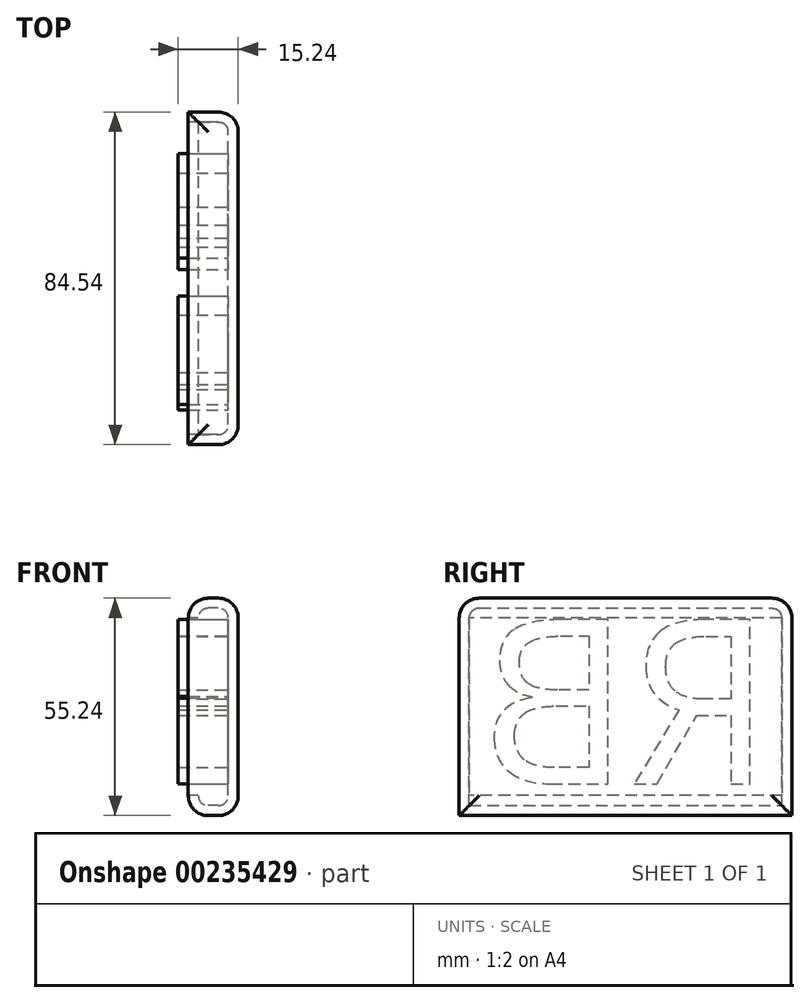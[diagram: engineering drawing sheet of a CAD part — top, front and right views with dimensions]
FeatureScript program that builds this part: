
annotation { "Feature Type Name" : "Feature", "Feature Type Description" : "" }
export const myFeature = defineFeature(function(context is Context, id is Id, definition is map)
    precondition{}
    {
        {
            var Q0;
            Q0=qCreatedBy(makeId("Right.planeOp"),FACE);
            var sketch = newSketch(context, id + "F0", { "sketchPlane" : qUnion([Q0])});
            skLineSegment(sketch, "E0.bottom", {"start": v(42.27, 27.62) * mm, "end": v(-42.27, 27.62) * mm});
            skLineSegment(sketch, "E0.top", {"start": v(42.27, -27.62) * mm, "end": v(-42.27, -27.62) * mm});
            skLineSegment(sketch, "E0.left", {"start": v(42.27, 27.62) * mm, "end": v(42.27, -27.62) * mm});
            skLineSegment(sketch, "E0.right", {"start": v(-42.27, 27.62) * mm, "end": v(-42.27, -27.62) * mm});
            skPoint(sketch, "E0.middle", {"position": v(0, 0) * mm});
            skSolve(sketch);
        }
        {
            var Q0;
            Q0=makeQuery(id+"F0.imprint","IMPRINT",FACE,{"disambiguationData":[TD([[makeQuery(id+"F0.imprint","IMPRINT",EDGE,{"derivedFrom":sQuery(id+"F0.wireOp",EDGE,"E0.bottom")}),1.0]])]});
            extrude(context, id + "F1", {"entities" : qUnion([Q0]), "depth" : 12.7 * mm});
        }
        {
            var Q0;
            Q0=makeQuery(id+"F1.opExtrude","SWEPT_FACE",FACE,{"disambiguationData":[OSD([sQuery(id+"F0.wireOp",EDGE,"E0.bottom")])]});
            var Q1;
            Q1=makeQuery(id+"F1.opExtrude","CAP_FACE",FACE,{"disambiguationData":[OSD([sQuery(id+"F0.wireOp",EDGE,"E0.bottom"),sQuery(id+"F0.wireOp",EDGE,"E0.top"),sQuery(id+"F0.wireOp",EDGE,"E0.left"),sQuery(id+"F0.wireOp",EDGE,"E0.right")])],"isStart":false});
            var Q2;
            Q2=makeQuery(id+"F1.opExtrude","CAP_EDGE",EDGE,{"disambiguationData":[OSD([sQuery(id+"F0.wireOp",EDGE,"E0.bottom")])],"isStart":false});
            fillet(context, id + "F2", {"entities" : qUnion([Q0, Q1, Q2]), "radius" : 5.08 * mm, "tangentPropagation" : true, "allowEdgeOverflow" : false});
        }
        {
            var Q0;
            Q0=makeQuery(id+"F1.opExtrude","CAP_EDGE",EDGE,{"disambiguationData":[OSD([sQuery(id+"F0.wireOp",EDGE,"E0.top")])],"isStart":true});
            fillet(context, id + "F3", {"entities" : qUnion([Q0]), "radius" : 5.08 * mm, "tangentPropagation" : true, "allowEdgeOverflow" : false});
        }
        {
            var Q0;
            Q0=makeQuery(id+"F1.opExtrude","CAP_FACE",FACE,{"disambiguationData":[OSD([sQuery(id+"F0.wireOp",EDGE,"E0.bottom"),sQuery(id+"F0.wireOp",EDGE,"E0.top"),sQuery(id+"F0.wireOp",EDGE,"E0.left"),sQuery(id+"F0.wireOp",EDGE,"E0.right")])],"isStart":true});
            shell(context, id + "F4", {"entities" : qUnion([Q0]), "thickness" : 2.54 * mm});
        }
        {
            var Q0;
            {var subQ0=sQuery(id+"F0.wireOp",EDGE,"E0.right");var subQ1=sQuery(id+"F0.wireOp",EDGE,"E0.left");var subQ2=sQuery(id+"F0.wireOp",EDGE,"E0.top");var subQ3=sQuery(id+"F0.wireOp",EDGE,"E0.bottom");Q0=makeQuery(id+"F4.opShell","OFFSET_FACE",FACE,{"disambiguationData":[OSD([subQ3,subQ2,subQ1,subQ0]),TDD([makeQuery(id+"F1.opExtrude","CAP_FACE",FACE,{"disambiguationData":[OSD([subQ3,subQ2,subQ1,subQ0])],"isStart":false})])]});}
            var sketch = newSketch(context, id + "F5", { "sketchPlane" : qUnion([Q0])});
            skText(sketch, "E1", { "text": "RB", "fontName": "OpenSans-Regular.ttf"});
            const initialGuessF5  = {"E1": [-0.03737, -0.01954, 1, 0, 0.04208]};
            skSetInitialGuess(sketch, initialGuessF5);
            skSolve(sketch);
        }
        {
            var Q0;
            Q0 = qSketchRegion(id + "F5", true);
            extrude(context, id + "F6", {"entities" : qUnion([Q0]), "operationType" : NewBodyOperationType.ADD, "depth" : 12.7 * mm});
        }
    });
